# Revit family: Сепаратор воздуха и шлама 1124
name_source: partatom
category: Rohrzubehör
units: mm (PartAtom-declared; Revit-internal decimal feet)

## family parameters
Arbeitsebenenbasiert = Nein
Beim Laden mit Abzugskörper schneiden = Nein
Bemaßung runder Anschluss = Durchmesser verwenden
Gemeinsam genutzt = Nein
Immer vertikal = Ja
OmniClass-Nummer = 23.65.55.14
OmniClass-Titel = Valves for Liquid Services
Teiletyp = Unterbricht

## types (1)
- Сепаратор воздуха и шлама 1124
    H01 = 158.5 mm  [stored 0.520013 ft]
    H02 = 92.5 mm  [stored 0.303478 ft]
    H03 = 10 mm  [stored 0.0328084 ft]
    H04 = 13.7 mm  [stored 0.0449475 ft]
    H05 = 66 mm  [stored 0.216535 ft]
    H06 = 56 mm  [stored 0.183727 ft]
    H07 = 24 mm  [stored 0.0787402 ft]
    H08 = 17 mm
    H09 = 13.3 mm  [stored 0.0436352 ft]
    H10 = 46 mm  [stored 0.150919 ft]
    H11 = 122 mm  [stored 0.400262 ft]
    H12 = 45.2 mm  [stored 0.148294 ft]
    H13 = 79.8 mm  [stored 0.261811 ft]
    Hersteller = Herz-Armaturen GmbH
    L01 = 61.9 mm  [stored 0.203084 ft]
    L02 = 70 mm  [stored 0.229659 ft]
    L03 = 102 mm  [stored 0.334646 ft]
    L04 = 49 mm  [stored 0.160761 ft]
    R01 = 50.5 mm  [stored 0.165682 ft]
    R02 = 43.5 mm  [stored 0.142717 ft]
    R03 = 14 mm  [stored 0.0459318 ft]
    R04 = 8.3 mm  [stored 0.027231 ft]
    R05 = 29 mm  [stored 0.0951444 ft]
    R06 = 21 mm  [stored 0.0688976 ft]
    R07 = 17 mm
    R08 = 34 mm
    R09 = 27.5 mm  [stored 0.0902231 ft]
    R10 = 20 mm  [stored 0.0656168 ft]
    R80 = 20 mm  [stored 0.0656168 ft]
    R90 = 1 mm  [stored 0.00328084 ft]
    R91 = 20.7 mm  [stored 0.0679134 ft]
    R92 = 5 mm  [stored 0.0164042 ft]
    S01 = 33.1 mm  [stored 0.108596 ft]
    S02 = 112 mm  [stored 0.367454 ft]
    S03 = 86 mm  [stored 0.282152 ft]
    S04 = 112.9 mm  [stored 0.370407 ft]
    SCRNCODE = 05;14;02
    SCRNSEQ = AWI;AWI_TYP="1016";2
    T01 = 43 mm  [stored 0.141076 ft]
    URL = www.herz-armaturen.ru
    VRL01 = 30 mm  [stored 0.0984252 ft]
    VRL02 = 13 mm
    VRL03 = 18 mm  [stored 0.0590551 ft]
    VRL04 = 8 mm  [stored 0.0262467 ft]
    VRL05 = 17 mm
    Vorgabe-Ansicht = 0 mm  [stored 0 ft]
    Корпус = Латунь, устойчивая к селективной цинковой коррозии
    Макс. рабочая температура = 110 °C
    Номинальное давление = 1000000.0 Pa
    Область применения = Сепаратор воздуха и шлама устанавливается в системах отопления или холодоснабжения и служит для отделения шлама и воздуха из теплоносителя системы отопления или холодоснабжения. Возможна установка как на вертикальных, так и горизонтальных трубопроводах.
    Рабочее давление = 600000.0 Pa

note: [stored X ft] marks values corroborated as IEEE doubles in the binary element streams (Revit-internal decimal feet)
